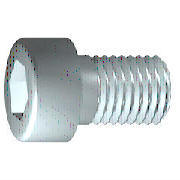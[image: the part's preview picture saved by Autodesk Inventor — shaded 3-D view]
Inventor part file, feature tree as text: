
AUTODESK INVENTOR PART (.ipt)
format: ipt  version: 2023.2 (Build 272271030, 271C)  size: 187,392 bytes
history: native  units: mm (DEFAULTED — no unit token found)
features: sketch x2, other x1, extrude x1, plane x1, fillet x1
ambient origin geometry x7: Origin, YZ Plane, XY Plane, X Axis, Y Axis, Z Axis, Center Point
bodies: Solid1 (feature_tree)
feature tree (6):
  other  "Körper"
  extrude  "Loch"  Depth=3.0mm
  plane  "Work Plane1"
  fillet  "Fillet2"  Radius=3.0mm
  sketch  "Skizze1"  dims[d1=18.0mm d2=0.306825mm d3=3.0mm]
  sketch  "Skizze2"  dims[d4=1.3mm d5=60.0deg d6=3.0mm d7=3.0mm d8=2.886751mm d9=5.5mm d10=90.0deg d11=10.0mm d12=0.0mm d13=18.0mm d14=0.0mm d15=0.306725mm d16=0.306725mm d17=0.3mm d19=0.0mm d26=25.0mm d27=45.0deg d28=0.0mm d29=0.0mm d30=0.1mm]
